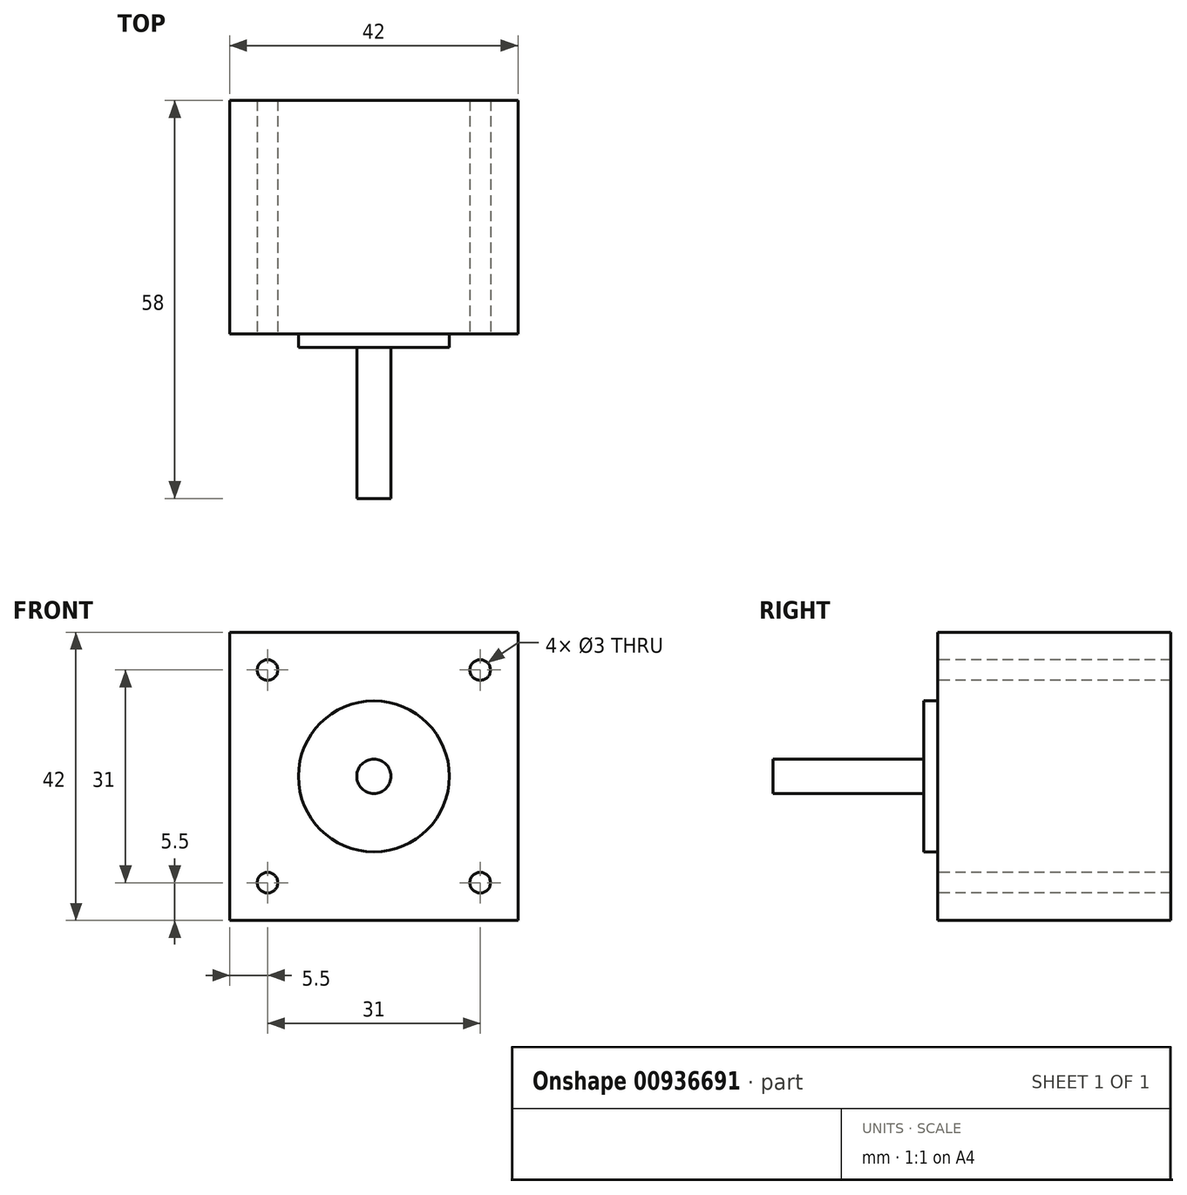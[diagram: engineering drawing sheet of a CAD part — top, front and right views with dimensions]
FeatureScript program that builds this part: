
annotation { "Feature Type Name" : "Feature", "Feature Type Description" : "" }
export const myFeature = defineFeature(function(context is Context, id is Id, definition is map)
    precondition{}
    {
        {
            var Q0;
            Q0=qCreatedBy(makeId("Front.planeOp"),FACE);
            var sketch = newSketch(context, id + "F0", { "sketchPlane" : qUnion([Q0])});
            skLineSegment(sketch, "E0.bottom", {"start": v(0, 0) * mm, "end": v(-42, 0) * mm});
            skLineSegment(sketch, "E0.top", {"start": v(0, 42) * mm, "end": v(-42, 42) * mm});
            skLineSegment(sketch, "E0.left", {"start": v(0, 0) * mm, "end": v(0, 42) * mm});
            skLineSegment(sketch, "E0.right", {"start": v(-42, 0) * mm, "end": v(-42, 42) * mm});
            skCircle(sketch, "E1", {"center": v(-21, 21) * mm, "radius": 11 * mm});
            skPoint(sketch, "E1.centerSnap0", {"position": v(0, 21) * mm});
            skPoint(sketch, "E1.centerSnap1", {"position": v(-21, 42) * mm});
            skCircle(sketch, "E2", {"center": v(-21, 21) * mm, "radius": 2.5 * mm});
            skCircle(sketch, "E3", {"center": v(-36.5, 36.5) * mm, "radius": 1.5 * mm});
            skCircle(sketch, "E4", {"center": v(-5.5, 36.5) * mm, "radius": 1.5 * mm});
            skCircle(sketch, "E5", {"center": v(-5.5, 5.5) * mm, "radius": 1.5 * mm});
            skCircle(sketch, "E6", {"center": v(-36.5, 5.5) * mm, "radius": 1.5 * mm});
            skSolve(sketch);
        }
        {
            var Q0;
            Q0=makeQuery(id+"F0.imprint","IMPRINT",FACE,{"disambiguationData":[TD([[makeQuery(id+"F0.imprint","IMPRINT",EDGE,{"derivedFrom":sQuery(id+"F0.wireOp",EDGE,"E0.bottom")}),-1.0]])]});
            var Q1;
            Q1=makeQuery(id+"F0.imprint","IMPRINT",FACE,{"disambiguationData":[TD([[makeQuery(id+"F0.imprint","IMPRINT",EDGE,{"derivedFrom":sQuery(id+"F0.wireOp",EDGE,"E1")}),1.0]])]});
            var Q2;
            Q2=makeQuery(id+"F0.imprint","IMPRINT",FACE,{"disambiguationData":[TD([[makeQuery(id+"F0.imprint","IMPRINT",EDGE,{"derivedFrom":sQuery(id+"F0.wireOp",EDGE,"E2")}),1.0]])]});
            extrude(context, id + "F1", {"entities" : qUnion([Q0, Q1, Q2]), "oppositeDirection" : true, "depth" : 34 * mm, "offsetDistance" : 25 * mm});
        }
        {
            var Q0;
            Q0=makeQuery(id+"F0.imprint","IMPRINT",FACE,{"disambiguationData":[TD([[makeQuery(id+"F0.imprint","IMPRINT",EDGE,{"derivedFrom":sQuery(id+"F0.wireOp",EDGE,"E2")}),1.0]])]});
            extrude(context, id + "F2", {"entities" : qUnion([Q0]), "operationType" : NewBodyOperationType.ADD, "depth" : 24 * mm, "offsetDistance" : 25 * mm});
        }
        {
            var Q0;
            Q0=makeQuery(id+"F0.imprint","IMPRINT",FACE,{"disambiguationData":[TD([[makeQuery(id+"F0.imprint","IMPRINT",EDGE,{"derivedFrom":sQuery(id+"F0.wireOp",EDGE,"E1")}),1.0]])]});
            extrude(context, id + "F3", {"entities" : qUnion([Q0]), "operationType" : NewBodyOperationType.ADD, "depth" : 2 * mm, "offsetDistance" : 25 * mm});
        }
    });
